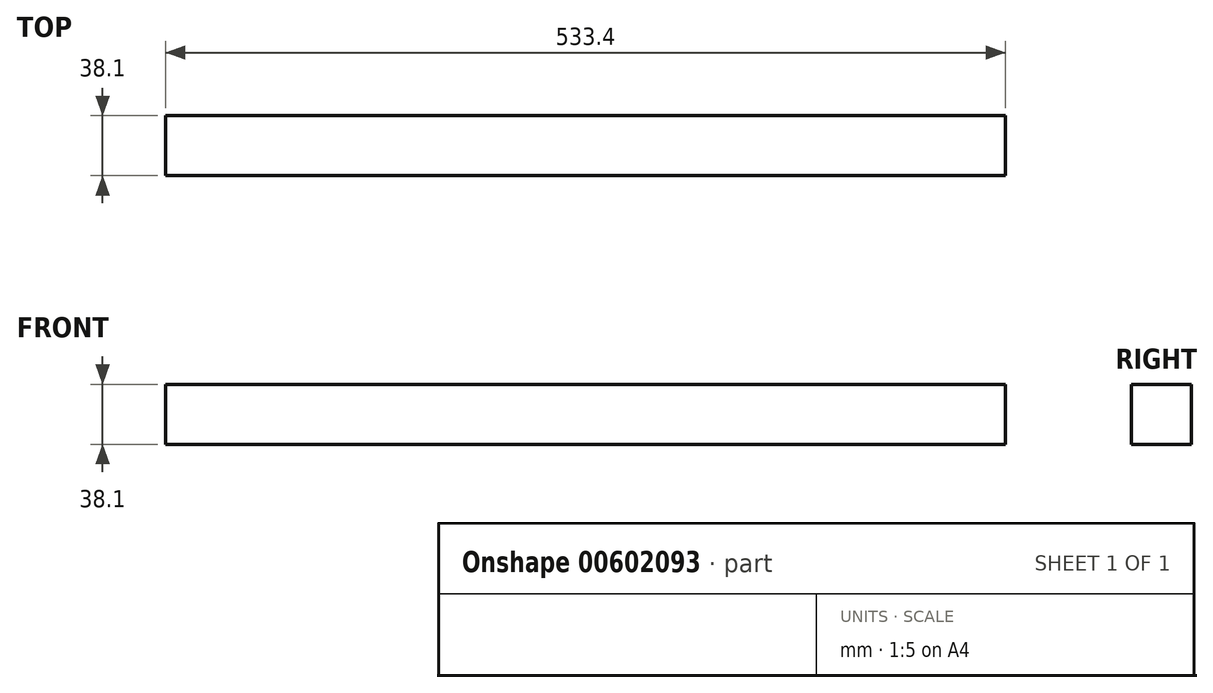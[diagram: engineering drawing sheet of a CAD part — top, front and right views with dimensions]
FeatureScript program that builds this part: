
annotation { "Feature Type Name" : "Feature", "Feature Type Description" : "" }
export const myFeature = defineFeature(function(context is Context, id is Id, definition is map)
    precondition{}
    {
        {
            var Q0;
            Q0=qCreatedBy(makeId("Right.planeOp"),FACE);
            var sketch = newSketch(context, id + "F0", { "sketchPlane" : qUnion([Q0])});
            skLineSegment(sketch, "E0.bottom", {"start": v(19.05, 19.05) * mm, "end": v(-19.05, 19.05) * mm});
            skLineSegment(sketch, "E0.top", {"start": v(19.05, -19.05) * mm, "end": v(-19.05, -19.05) * mm});
            skLineSegment(sketch, "E0.left", {"start": v(19.05, 19.05) * mm, "end": v(19.05, -19.05) * mm});
            skLineSegment(sketch, "E0.right", {"start": v(-19.05, 19.05) * mm, "end": v(-19.05, -19.05) * mm});
            skPoint(sketch, "E0.middle", {"position": v(0, 0) * mm});
            skSolve(sketch);
        }
        {
            var Q0;
            Q0 = qSketchRegion(id + "F0", true);
            extrude(context, id + "F1", {"entities" : qUnion([Q0]), "depth" : 533.4 * mm, "offsetDistance" : 25.4 * mm});
        }
    });
